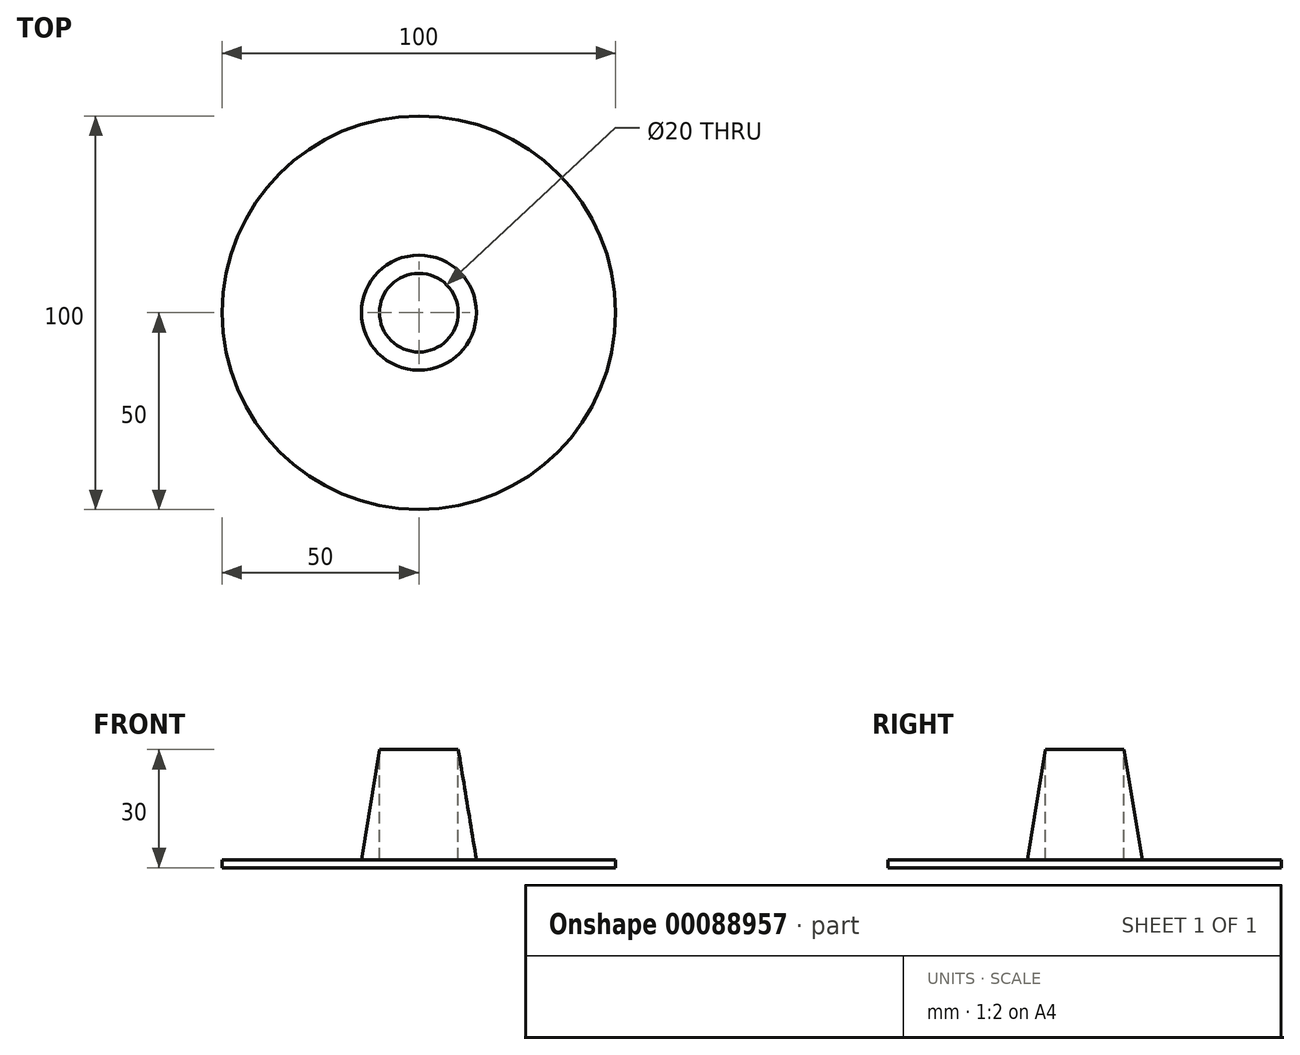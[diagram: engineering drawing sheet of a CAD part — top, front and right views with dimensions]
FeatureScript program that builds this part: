
annotation { "Feature Type Name" : "Feature", "Feature Type Description" : "" }
export const myFeature = defineFeature(function(context is Context, id is Id, definition is map)
    precondition{}
    {
        {
            var Q0;
            Q0=qCreatedBy(makeId("Front.planeOp"),FACE);
            var sketch = newSketch(context, id + "F0", { "sketchPlane" : qUnion([Q0])});
            skLineSegment(sketch, "E0", {"start": v(0, 0) * mm, "end": v(-50, 0) * mm});
            skLineSegment(sketch, "E1", {"start": v(-50, 0) * mm, "end": v(-50, 2) * mm});
            skLineSegment(sketch, "E2", {"start": v(-50, 2) * mm, "end": v(-14.62, 2) * mm});
            skLineSegment(sketch, "E3", {"start": v(-14.62, 2) * mm, "end": v(-10, 30) * mm});
            skLineSegment(sketch, "E4", {"start": v(0, 2) * mm, "end": v(0, 0) * mm});
            skLineSegment(sketch, "E5", {"start": v(-10, 30) * mm, "end": v(-10, 1.98) * mm});
            skLineSegment(sketch, "E6", {"start": v(-10, 1.98) * mm, "end": v(0, 2) * mm});
            skSolve(sketch);
        }
        {
            var Q0;
            Q0=makeQuery(id+"F0.imprint","IMPRINT",FACE,{"disambiguationData":[TD([[makeQuery(id+"F0.imprint","IMPRINT",EDGE,{"derivedFrom":sQuery(id+"F0.wireOp",EDGE,"E0")}),-1.0]])]});
            var Q1;
            Q1=sQuery(id+"F0.wireOp",EDGE,"E4");
            revolve(context, id + "F1", {"entities" : qUnion([Q0]), "axis" : qUnion([Q1]), "revolveType" : RevolveType.FULL});
        }
    });
